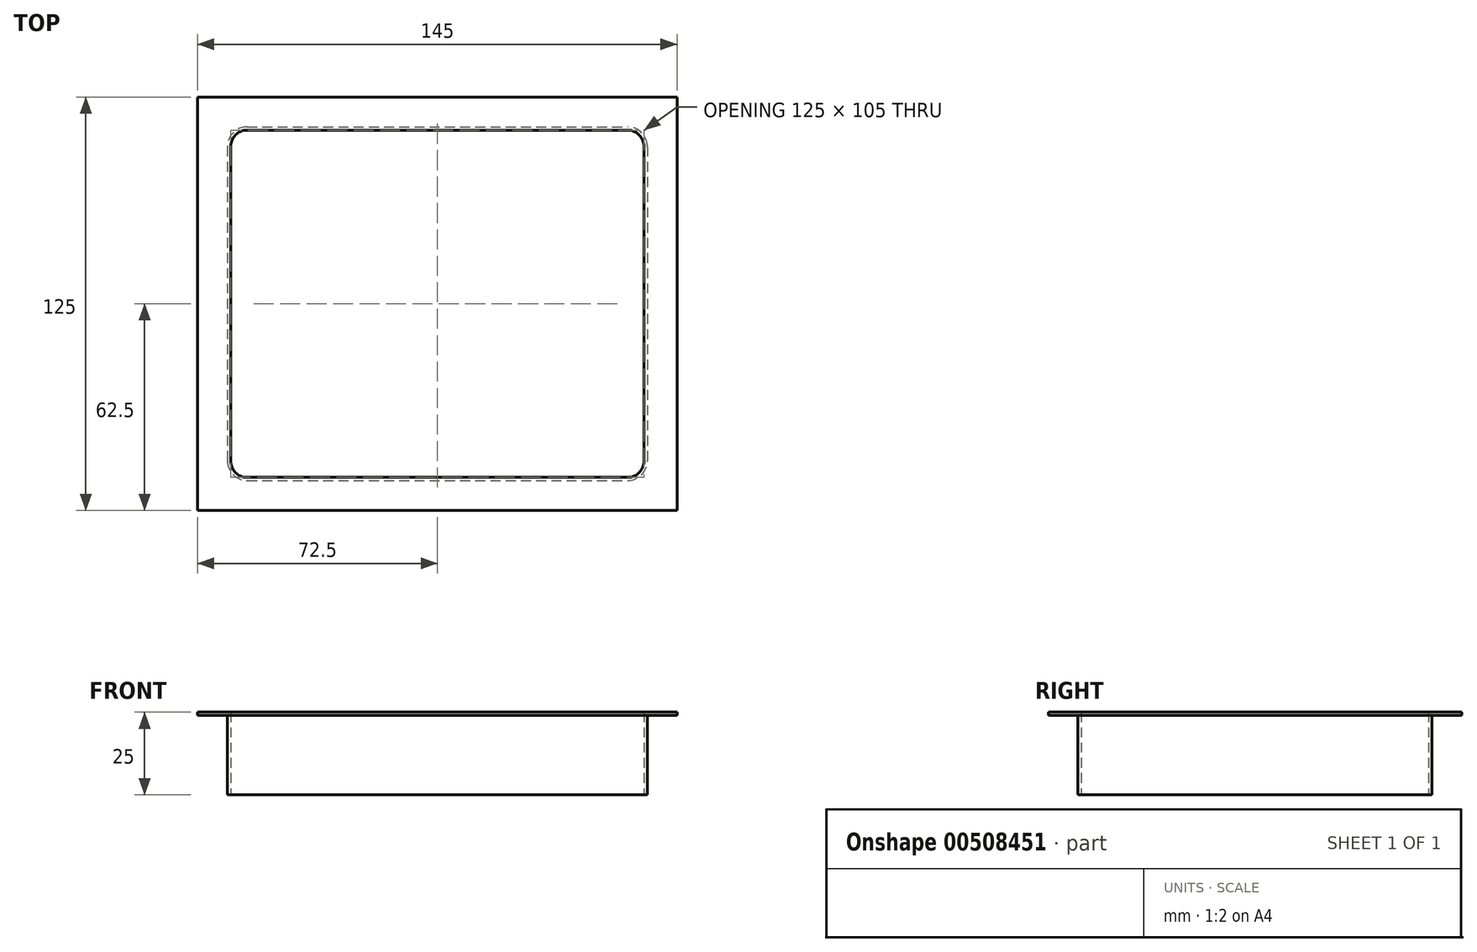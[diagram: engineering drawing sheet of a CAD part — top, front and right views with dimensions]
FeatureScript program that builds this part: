
annotation { "Feature Type Name" : "Feature", "Feature Type Description" : "" }
export const myFeature = defineFeature(function(context is Context, id is Id, definition is map)
    precondition{}
    {
        {
            var Q0;
            Q0=qCreatedBy(makeId("Top.planeOp"),FACE);
            var sketch = newSketch(context, id + "F0", { "sketchPlane" : qUnion([Q0])});
            skLineSegment(sketch, "E0.bottom", {"start": v(-62.5, 52.5) * mm, "end": v(62.5, 52.5) * mm});
            skLineSegment(sketch, "E0.top", {"start": v(-62.5, -52.5) * mm, "end": v(62.5, -52.5) * mm});
            skLineSegment(sketch, "E0.left", {"start": v(-62.5, 52.5) * mm, "end": v(-62.5, -52.5) * mm});
            skLineSegment(sketch, "E0.right", {"start": v(62.5, 52.5) * mm, "end": v(62.5, -52.5) * mm});
            skPoint(sketch, "E0.middle", {"position": v(0, 0) * mm});
            skLineSegment(sketch, "E1.0", {"start": v(-72.5, -62.5) * mm, "end": v(72.5, -62.5) * mm});
            skLineSegment(sketch, "E1.1", {"start": v(-72.5, 62.5) * mm, "end": v(-72.5, -62.5) * mm});
            skLineSegment(sketch, "E1.2", {"start": v(-72.5, 62.5) * mm, "end": v(72.5, 62.5) * mm});
            skLineSegment(sketch, "E1.3", {"start": v(72.5, 62.5) * mm, "end": v(72.5, -62.5) * mm});
            skSolve(sketch);
        }
        {
            var Q0;
            Q0=makeQuery(id+"F0.imprint","IMPRINT",FACE,{"disambiguationData":[TD([[makeQuery(id+"F0.imprint","IMPRINT",EDGE,{"derivedFrom":sQuery(id+"F0.wireOp",EDGE,"E0.bottom")}),1.0]])]});
            extrude(context, id + "F1", {"entities" : qUnion([Q0]), "depth" : 1 * mm});
        }
        {
            var Q0;
            Q0=makeQuery(id+"F1.opExtrude","SWEPT_EDGE",EDGE,{"disambiguationData":[OSD([sQuery(id+"F0.wireOp",EDGE,"E0.bottom"),sQuery(id+"F0.wireOp",EDGE,"E0.left")])]});
            var Q1;
            Q1=makeQuery(id+"F1.opExtrude","SWEPT_EDGE",EDGE,{"disambiguationData":[OSD([sQuery(id+"F0.wireOp",EDGE,"E0.top"),sQuery(id+"F0.wireOp",EDGE,"E0.left")])]});
            var Q2;
            Q2=makeQuery(id+"F1.opExtrude","SWEPT_EDGE",EDGE,{"disambiguationData":[OSD([sQuery(id+"F0.wireOp",EDGE,"E0.top"),sQuery(id+"F0.wireOp",EDGE,"E0.right")])]});
            var Q3;
            Q3=makeQuery(id+"F1.opExtrude","SWEPT_EDGE",EDGE,{"disambiguationData":[OSD([sQuery(id+"F0.wireOp",EDGE,"E0.bottom"),sQuery(id+"F0.wireOp",EDGE,"E0.right")])]});
            fillet(context, id + "F2", {"entities" : qUnion([Q0, Q1, Q2, Q3]), "radius" : 5 * mm, "tangentPropagation" : true, "allowEdgeOverflow" : false});
        }
        {
            var Q0;
            Q0=makeQuery(id+"F1.opExtrude","CAP_FACE",FACE,{"disambiguationData":[OSD([sQuery(id+"F0.wireOp",EDGE,"E0.bottom"),sQuery(id+"F0.wireOp",EDGE,"E0.top"),sQuery(id+"F0.wireOp",EDGE,"E0.left"),sQuery(id+"F0.wireOp",EDGE,"E0.right"),sQuery(id+"F0.wireOp",EDGE,"E1.0"),sQuery(id+"F0.wireOp",EDGE,"E1.1"),sQuery(id+"F0.wireOp",EDGE,"E1.2"),sQuery(id+"F0.wireOp",EDGE,"E1.3")])],"isStart":false});
            var sketch = newSketch(context, id + "F3", { "sketchPlane" : qUnion([Q0])});
            skLineSegment(sketch, "E2.0", {"start": v(-63.5, 47.5) * mm, "end": v(-63.5, -47.5) * mm});
            skArc(sketch, "E2.1", {"start": v(-57.5, -53.5) * mm, "mid": v(-61.74, -51.74) * mm, "end": v(-63.5, -47.5) * mm});
            skArc(sketch, "E2.2", {"start": v(-63.5, 47.5) * mm, "mid": v(-61.74, 51.74) * mm, "end": v(-57.5, 53.5) * mm});
            skLineSegment(sketch, "E2.3", {"start": v(-57.5, -53.5) * mm, "end": v(57.5, -53.5) * mm});
            skLineSegment(sketch, "E2.4", {"start": v(-57.5, 53.5) * mm, "end": v(57.5, 53.5) * mm});
            skArc(sketch, "E2.5", {"start": v(57.5, 53.5) * mm, "mid": v(61.74, 51.74) * mm, "end": v(63.5, 47.5) * mm});
            skLineSegment(sketch, "E2.6", {"start": v(63.5, 47.5) * mm, "end": v(63.5, -47.5) * mm});
            skArc(sketch, "E2.7", {"start": v(63.5, -47.5) * mm, "mid": v(61.74, -51.74) * mm, "end": v(57.5, -53.5) * mm});
            skSolve(sketch);
        }
        {
            var Q0;
            Q0=makeQuery(id+"F3.imprint","IMPRINT",FACE,{"disambiguationData":[TD([[makeQuery(id+"F3.imprint","IMPRINT",EDGE,{"derivedFrom":sQuery(id+"F3.wireOp",EDGE,"E2.0")}),1.0]])]});
            extrude(context, id + "F4", {"entities" : qUnion([Q0]), "operationType" : NewBodyOperationType.ADD, "oppositeDirection" : true, "depth" : 25 * mm});
        }
    });
